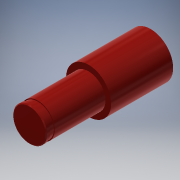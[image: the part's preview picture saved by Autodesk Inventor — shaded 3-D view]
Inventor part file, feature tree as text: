
AUTODESK INVENTOR PART (.ipt)
format: ipt  version: 2018 (Build 220112000, 112)  size: 122,368 bytes
history: native  units: mm
features: revolve x1, sketch x1
ambient origin geometry x8: Origin, YZ Plane, XZ Plane, XY Plane, X Axis, Y Axis, Z Axis, Center Point
bodies: Solid1 (feature_tree)
feature tree (2):
  revolve  "Revolution1"  [1 undecoded]
  sketch  "Sketch1"  dims[d0=21.5mm d1=0.15mm d2=0.15mm d3=0.7mm d4=0.15mm d5=0.8mm d6=11.0mm d7=9.0mm d8=4.0mm d9=3.0mm d10=90.0deg]
note: 1 required parameter value undecoded (feature->parameter linkage not recoverable at this tier; creation-order binding heuristic only, values carry confidence <= 0.55)
